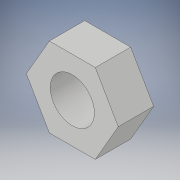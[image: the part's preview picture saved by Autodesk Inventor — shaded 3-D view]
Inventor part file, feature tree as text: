
AUTODESK INVENTOR PART (.ipt)
format: ipt  version: 2018 (Build 220112000, 112)  size: 99,328 bytes
history: native  units: in
note: dims shown in document units (in); Inventor stores cm internally (conversion verified against a paired STEP export)
features: extrude x1, sketch x1
ambient origin geometry x8: Origin, YZ Plane, XZ Plane, XY Plane, X Axis, Y Axis, Z Axis, Center Point
bodies: Solid1 (feature_tree)
feature tree (2):
  extrude  "Extrusion1"  Depth=0.2in
  sketch  "Sketch1"  dims[d0=0.45in d1=0.25in d2=0.2in d3=0.0in]
